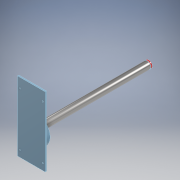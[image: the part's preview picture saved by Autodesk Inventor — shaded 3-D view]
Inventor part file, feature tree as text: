
AUTODESK INVENTOR PART (.ipt)
format: ipt  version: 2022 (Build 260153000, 153)  size: 144,896 bytes
history: native  units: mm
features: sketch x5, extrude x4, hole x1
ambient origin geometry x8: Origin, YZ Plane, XZ Plane, XY Plane, X Axis, Y Axis, Z Axis, Center Point
bodies: Solid1 (feature_tree)
feature tree (10):
  extrude  "Connector"  Depth=624.0mm TaperAngle=0.0deg
  extrude  "RotAxis"  Depth=8.0mm TaperAngle=0.0deg
  extrude  "TelescopeMount"  [1 undecoded]
  extrude  "Cap"  [1 undecoded]
  hole  "Hole1"  [1 undecoded]
  sketch  "Sketch1"  dims[d0=20.0mm d1=0.0mm d2=624.0mm d3=0.0mm]
  sketch  "Sketch2"  dims[d4=8.0mm d5=0.0mm d6=8.0mm d7=0.0mm]
  sketch  "Sketch3"  dims[d8=6.647mm d9=16.0mm d10=4.0mm d11=2.0mm d12=90.0deg d13=20.0mm d14=20.594885mm]
  sketch  "Sketch4"
  sketch  "Sketch5"
note: 3 required parameter values undecoded (feature->parameter linkage not recoverable at this tier; creation-order binding heuristic only, values carry confidence <= 0.55)
